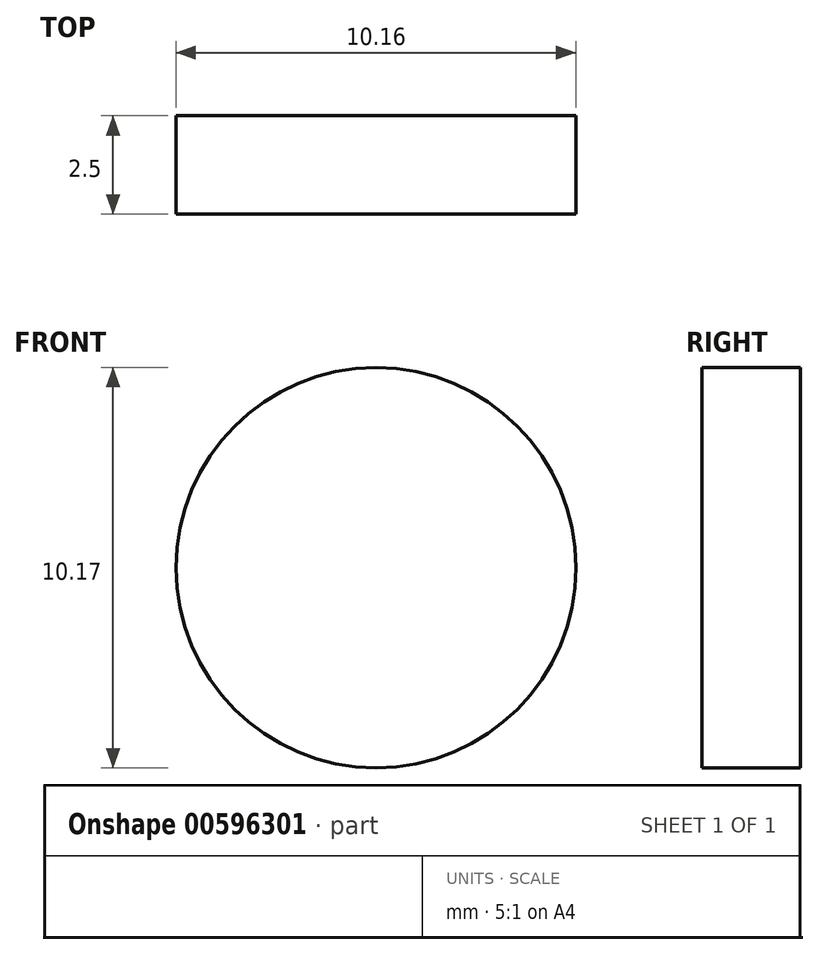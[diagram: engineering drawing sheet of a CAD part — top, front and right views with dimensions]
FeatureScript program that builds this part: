
annotation { "Feature Type Name" : "Feature", "Feature Type Description" : "" }
export const myFeature = defineFeature(function(context is Context, id is Id, definition is map)
    precondition{}
    {
        {
            var Q0;
            Q0=qCreatedBy(makeId("Front.planeOp"),FACE);
            var sketch = newSketch(context, id + "F0", { "sketchPlane" : qUnion([Q0])});
            skCircle(sketch, "E0", {"center": v(-39.26, 17.28) * mm, "radius": 5.08 * mm});
            skSolve(sketch);
        }
        {
            var Q0;
            Q0 = qSketchRegion(id + "F0", true);
            extrude(context, id + "F1", {"entities" : qUnion([Q0]), "depth" : 2.5 * mm, "offsetDistance" : 25 * mm});
        }
    });
